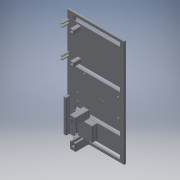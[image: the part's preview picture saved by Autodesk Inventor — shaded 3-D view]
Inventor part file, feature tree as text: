
AUTODESK INVENTOR PART (.ipt)
format: ipt  version: 2018 (Build 220112000, 112)  size: 982,016 bytes
history: native  units: in
note: dims shown in document units (in); Inventor stores cm internally (conversion verified against a paired STEP export)
features: reference x20, extrude x8, sketch x8, other x8, fillet x7, plane x6, projected_geometry x1
ambient origin geometry x8: Origin, YZ Plane, XZ Plane, XY Plane, X Axis, Y Axis, Z Axis, Center Point
bodies: Solid1 (feature_tree)
feature tree (58):
  extrude  "Extrusion1"  Depth=0.2839in
  sketch  "Sketch2"  dims[d6=0.2839in d7=2.1654in]
  plane  "Work Plane1"
  extrude  "Extrusion2"  Depth=2.1654in
  extrude  "Extrusion3"  Depth=0.1969in
  sketch  "Sketch4"  dims[d12=0.1969in d14=0.1181in d15=0.0in]
  plane  "Work Plane2"
  extrude  "Extrusion4"  Depth=0.1181in TaperAngle=0.0deg
  sketch  "Sketch5"  dims[d16=0.0098in d17=0.1969in]
  plane  "Work Plane3"
  extrude  "Extrusion5"  Depth=0.1969in
  sketch  "Sketch6"  dims[d18=1.0in d19=0.0in d20=0.1969in d21=0.0in]
  plane  "Work Plane4"
  extrude  "Extrusion6"  Depth=0.1969in TaperAngle=0.0deg
  sketch  "Sketch7"  dims[d22=0.0098in d23=2.0in]
  plane  "Work Plane5"
  extrude  "Extrusion7"  Depth=2.0in
  sketch  "Sketch8"  dims[d24=0.1969in d25=0.0in d27=0.1969in d28=0.0098in d29=0.0098in d30=0.0692in d31=0.1181in d32=0.1969in d33=0.0in d34=0.1969in d35=0.0in d36=0.1969in d37=0.0in d38=0.0098in d39=0.0098in d42=0.1575in d43=0.0098in d44=0.0098in d45=0.1575in d46=0.0787in d48=0.0787in d49=0.0787in d50=0.0787in d51=0.0787in d52=0.1969in d53=0.0in d54=0.0394in d55=0.0394in d56=0.0394in d57=0.0394in d58=0.0394in d59=0.0394in d60=0.0394in]
  plane  "Work Plane6"
  extrude  "Extrusion8"  Depth=0.0394in
  fillet  "Fillet1"  Radius=0.0098in
  fillet  "Fillet2"  Radius=0.0098in
  fillet  "Fillet3"  Radius=0.0692in
  fillet  "Fillet4"  Radius=0.1181in
  fillet  "Fillet5"  Radius=0.1969in
  fillet  "Fillet6"  Radius=0.1969in
  fillet  "Fillet7"  Radius=0.1969in
  sketch  "Sketch1"  dims[d3=1.0236in d5=0.2839in]
  reference  "Reference2"
  reference  "Reference3"
  sketch  "Sketch3"  dims[d8=0.1969in d9=0.1969in]
  projected_geometry  "Projected Loop1"
  reference  "Reference4"
  reference  "Reference5"
  reference  "Reference6"
  reference  "Reference7"
  reference  "Reference8"
  reference  "Reference9"
  reference  "Reference10"
  reference  "Reference11"
  reference  "Reference12"
  reference  "Reference13"
  reference  "Reference14"
  reference  "Reference15"
  reference  "Reference16"
  reference  "Reference17"
  reference  "Reference18"
  reference  "Reference19"
  reference  "Reference20"
  reference  "Reference21"
  other  "<userpath>\OneDrive\Documents\Inventor\TSA\2018\Animatronics\Tortoise\TurtleAssembly2.iam"
  other  "TurtleAssembly2.iam"
  other  "arduino uno:3"
  other  "PCB_Final_Default:1"
  other  "HeadOpenRack:3"
  other  "servo (2):9"
  other  "Frame - Copy:1"
  other  "SyringeAttachment:7"
